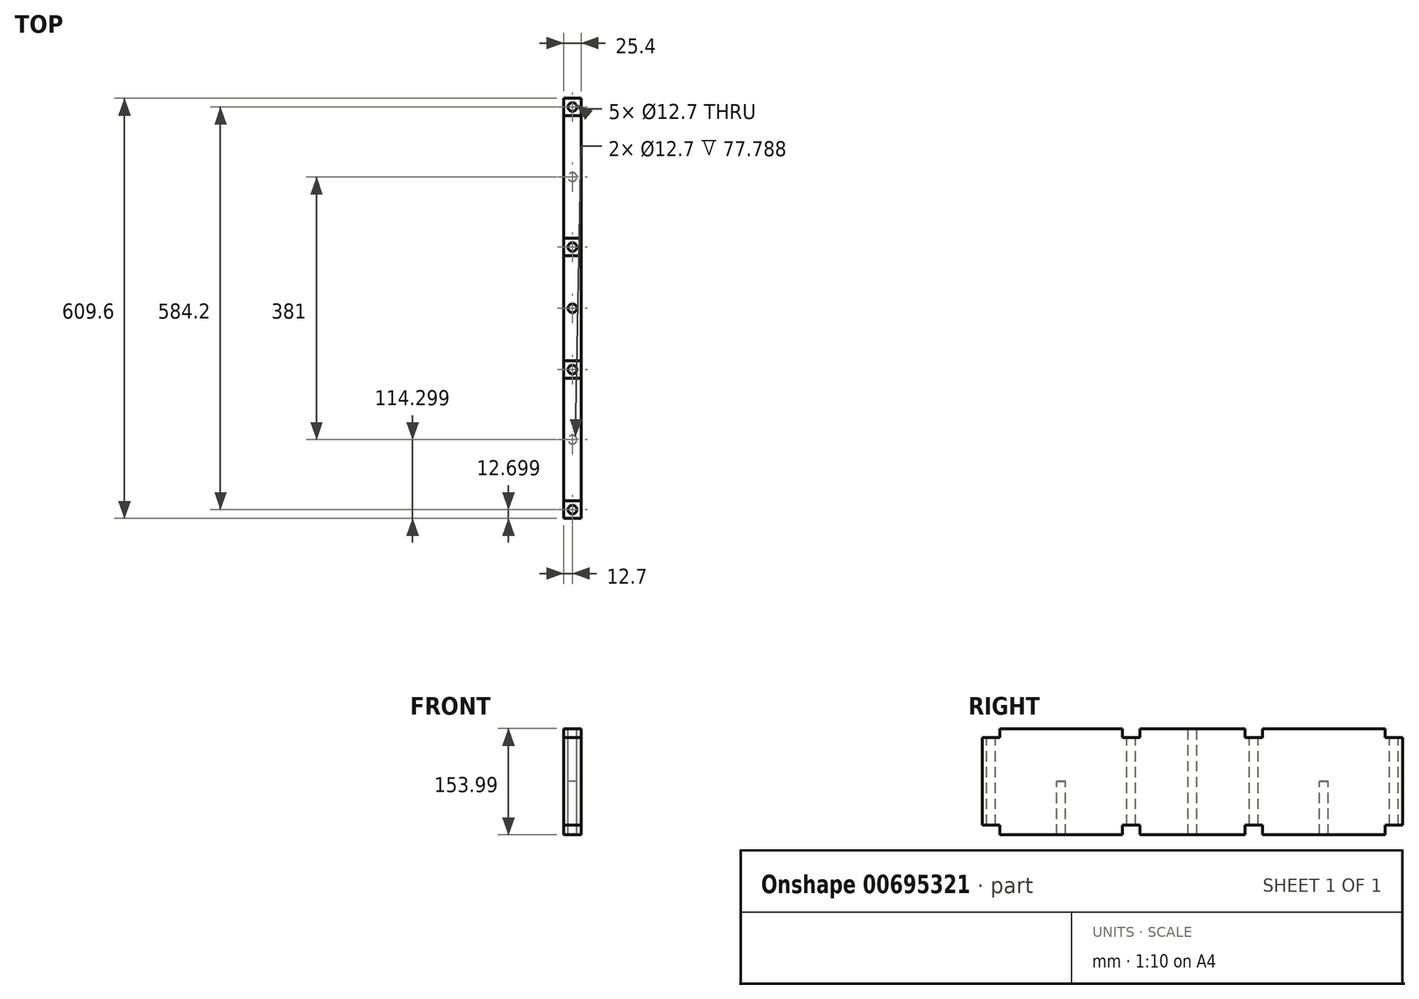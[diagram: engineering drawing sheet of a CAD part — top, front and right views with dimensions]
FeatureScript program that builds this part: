
annotation { "Feature Type Name" : "Feature", "Feature Type Description" : "" }
export const myFeature = defineFeature(function(context is Context, id is Id, definition is map)
    precondition{}
    {
        {
            var Q0;
            Q0=qCreatedBy(makeId("Right.planeOp"),FACE);
            var sketch = newSketch(context, id + "F0", { "sketchPlane" : qUnion([Q0])});
            skLineSegment(sketch, "E0.bottom", {"start": v(-308, -56.05) * mm, "end": v(301.6, -56.05) * mm});
            skLineSegment(sketch, "E0.top", {"start": v(-308, -210.04) * mm, "end": v(301.6, -210.04) * mm});
            skLineSegment(sketch, "E0.left", {"start": v(-308, -56.05) * mm, "end": v(-308, -210.04) * mm});
            skLineSegment(sketch, "E0.right", {"start": v(301.6, -56.05) * mm, "end": v(301.6, -210.04) * mm});
            skSolve(sketch);
        }
        {
            var Q0;
            Q0=makeQuery(id+"F0.imprint","IMPRINT",FACE,{"disambiguationData":[TD([[makeQuery(id+"F0.imprint","IMPRINT",EDGE,{"derivedFrom":sQuery(id+"F0.wireOp",EDGE,"E0.bottom")}),-1.0]])]});
            extrude(context, id + "F1", {"entities" : qUnion([Q0]), "depth" : 25.4 * mm, "offsetDistance" : 25.4 * mm});
        }
        {
            var Q0;
            Q0=makeQuery(id+"F1.opExtrude","CAP_FACE",FACE,{"disambiguationData":[OSD([sQuery(id+"F0.wireOp",EDGE,"E0.bottom"),sQuery(id+"F0.wireOp",EDGE,"E0.top"),sQuery(id+"F0.wireOp",EDGE,"E0.left"),sQuery(id+"F0.wireOp",EDGE,"E0.right")])],"isStart":false});
            var sketch = newSketch(context, id + "F2", { "sketchPlane" : qUnion([Q0])});
            skLineSegment(sketch, "E1.bottom", {"start": v(-308, -210.04) * mm, "end": v(-282.6, -210.04) * mm});
            skLineSegment(sketch, "E1.top", {"start": v(-308, -194.17) * mm, "end": v(-282.6, -194.17) * mm});
            skLineSegment(sketch, "E1.left", {"start": v(-308, -210.04) * mm, "end": v(-308, -194.17) * mm});
            skLineSegment(sketch, "E1.right", {"start": v(-282.6, -210.04) * mm, "end": v(-282.6, -194.17) * mm});
            skLineSegment(sketch, "E2.bottom", {"start": v(-104.8, -210.04) * mm, "end": v(-79.4, -210.04) * mm});
            skLineSegment(sketch, "E2.top", {"start": v(-104.8, -194.17) * mm, "end": v(-79.4, -194.17) * mm});
            skLineSegment(sketch, "E2.left", {"start": v(-104.8, -210.04) * mm, "end": v(-104.8, -194.17) * mm});
            skLineSegment(sketch, "E2.right", {"start": v(-79.4, -210.04) * mm, "end": v(-79.4, -194.17) * mm});
            skLineSegment(sketch, "E3.bottom", {"start": v(73, -210.04) * mm, "end": v(98.4, -210.04) * mm});
            skLineSegment(sketch, "E3.top", {"start": v(73, -194.17) * mm, "end": v(98.4, -194.17) * mm});
            skLineSegment(sketch, "E3.left", {"start": v(73, -210.04) * mm, "end": v(73, -194.17) * mm});
            skLineSegment(sketch, "E3.right", {"start": v(98.4, -210.04) * mm, "end": v(98.4, -194.17) * mm});
            skLineSegment(sketch, "E4.bottom", {"start": v(301.6, -210.04) * mm, "end": v(276.2, -210.04) * mm});
            skLineSegment(sketch, "E4.top", {"start": v(301.6, -194.17) * mm, "end": v(276.2, -194.17) * mm});
            skLineSegment(sketch, "E4.left", {"start": v(301.6, -210.04) * mm, "end": v(301.6, -194.17) * mm});
            skLineSegment(sketch, "E4.right", {"start": v(276.2, -210.04) * mm, "end": v(276.2, -194.17) * mm});
            skLineSegment(sketch, "E5.bottom", {"start": v(-308, -56.05) * mm, "end": v(-282.6, -56.05) * mm});
            skLineSegment(sketch, "E5.top", {"start": v(-308, -68.75) * mm, "end": v(-282.6, -68.75) * mm});
            skLineSegment(sketch, "E5.left", {"start": v(-308, -56.05) * mm, "end": v(-308, -68.75) * mm});
            skLineSegment(sketch, "E5.right", {"start": v(-282.6, -56.05) * mm, "end": v(-282.6, -68.75) * mm});
            skLineSegment(sketch, "E6.bottom", {"start": v(-104.8, -56.05) * mm, "end": v(-79.4, -56.05) * mm});
            skLineSegment(sketch, "E6.top", {"start": v(-104.8, -68.75) * mm, "end": v(-79.4, -68.75) * mm});
            skLineSegment(sketch, "E6.left", {"start": v(-104.8, -56.05) * mm, "end": v(-104.8, -68.75) * mm});
            skLineSegment(sketch, "E6.right", {"start": v(-79.4, -56.05) * mm, "end": v(-79.4, -68.75) * mm});
            skLineSegment(sketch, "E7.bottom", {"start": v(73, -56.05) * mm, "end": v(98.4, -56.05) * mm});
            skLineSegment(sketch, "E7.top", {"start": v(73, -68.75) * mm, "end": v(98.4, -68.75) * mm});
            skLineSegment(sketch, "E7.left", {"start": v(73, -56.05) * mm, "end": v(73, -68.75) * mm});
            skLineSegment(sketch, "E7.right", {"start": v(98.4, -56.05) * mm, "end": v(98.4, -68.75) * mm});
            skLineSegment(sketch, "E8.bottom", {"start": v(301.6, -56.05) * mm, "end": v(276.2, -56.05) * mm});
            skLineSegment(sketch, "E8.top", {"start": v(301.6, -68.75) * mm, "end": v(276.2, -68.75) * mm});
            skLineSegment(sketch, "E8.left", {"start": v(301.6, -56.05) * mm, "end": v(301.6, -68.75) * mm});
            skLineSegment(sketch, "E8.right", {"start": v(276.2, -56.05) * mm, "end": v(276.2, -68.75) * mm});
            skSolve(sketch);
        }
        {
            var Q0;
            Q0=makeQuery(id+"F2.imprint","IMPRINT",FACE,{"disambiguationData":[TD([[makeQuery(id+"F2.imprint","IMPRINT",EDGE,{"derivedFrom":sQuery(id+"F2.wireOp",EDGE,"E5.bottom")}),-1.0]])]});
            var Q1;
            Q1=makeQuery(id+"F2.imprint","IMPRINT",FACE,{"disambiguationData":[TD([[makeQuery(id+"F2.imprint","IMPRINT",EDGE,{"derivedFrom":sQuery(id+"F2.wireOp",EDGE,"E1.bottom")}),1.0]])]});
            var Q2;
            Q2=makeQuery(id+"F2.imprint","IMPRINT",FACE,{"disambiguationData":[TD([[makeQuery(id+"F2.imprint","IMPRINT",EDGE,{"derivedFrom":sQuery(id+"F2.wireOp",EDGE,"E2.bottom")}),1.0]])]});
            var Q3;
            Q3=makeQuery(id+"F2.imprint","IMPRINT",FACE,{"disambiguationData":[TD([[makeQuery(id+"F2.imprint","IMPRINT",EDGE,{"derivedFrom":sQuery(id+"F2.wireOp",EDGE,"E6.bottom")}),-1.0]])]});
            var Q4;
            Q4=makeQuery(id+"F2.imprint","IMPRINT",FACE,{"disambiguationData":[TD([[makeQuery(id+"F2.imprint","IMPRINT",EDGE,{"derivedFrom":sQuery(id+"F2.wireOp",EDGE,"E7.bottom")}),-1.0]])]});
            var Q5;
            Q5=makeQuery(id+"F2.imprint","IMPRINT",FACE,{"disambiguationData":[TD([[makeQuery(id+"F2.imprint","IMPRINT",EDGE,{"derivedFrom":sQuery(id+"F2.wireOp",EDGE,"E3.bottom")}),1.0]])]});
            var Q6;
            Q6=makeQuery(id+"F2.imprint","IMPRINT",FACE,{"disambiguationData":[TD([[makeQuery(id+"F2.imprint","IMPRINT",EDGE,{"derivedFrom":sQuery(id+"F2.wireOp",EDGE,"E8.bottom")}),-1.0]])]});
            var Q7;
            Q7=makeQuery(id+"F2.imprint","IMPRINT",FACE,{"disambiguationData":[TD([[makeQuery(id+"F2.imprint","IMPRINT",EDGE,{"derivedFrom":sQuery(id+"F2.wireOp",EDGE,"E4.bottom")}),1.0]])]});
            extrude(context, id + "F3", {"entities" : qUnion([Q0, Q1, Q2, Q3, Q4, Q5, Q6, Q7]), "operationType" : NewBodyOperationType.REMOVE, "oppositeDirection" : true, "depth" : 25.4 * mm, "offsetDistance" : 25.4 * mm});
        }
        {
            var Q0;
            Q0=makeQuery(id+"F3.boolean.opBoolean","COPY",FACE,{"derivedFrom":makeQuery(id+"F3.opExtrude","SWEPT_FACE",FACE,{"disambiguationData":[OSD([sQuery(id+"F2.wireOp",EDGE,"E5.top")])]})});
            var sketch = newSketch(context, id + "F4", { "sketchPlane" : qUnion([Q0])});
            skCircle(sketch, "E9", {"center": v(12.7, -295.3) * mm, "radius": 6.35 * mm});
            skPoint(sketch, "E9.centerSnap0", {"position": v(25.4, -295.3) * mm});
            skPoint(sketch, "E9.centerSnap1", {"position": v(12.7, -308) * mm});
            skSolve(sketch);
        }
        {
            var Q0;
            Q0=makeQuery(id+"F3.boolean.opBoolean","COPY",FACE,{"derivedFrom":makeQuery(id+"F3.opExtrude","SWEPT_FACE",FACE,{"disambiguationData":[OSD([sQuery(id+"F2.wireOp",EDGE,"E6.top")])]})});
            var sketch = newSketch(context, id + "F5", { "sketchPlane" : qUnion([Q0])});
            skCircle(sketch, "E10", {"center": v(12.7, -92.1) * mm, "radius": 6.35 * mm});
            skPoint(sketch, "E10.centerSnap0", {"position": v(25.4, -92.1) * mm});
            skPoint(sketch, "E10.centerSnap1", {"position": v(12.7, -79.4) * mm});
            skSolve(sketch);
        }
        {
            var Q0;
            Q0=makeQuery(id+"F3.boolean.opBoolean","COPY",FACE,{"derivedFrom":makeQuery(id+"F3.opExtrude","SWEPT_FACE",FACE,{"disambiguationData":[OSD([sQuery(id+"F2.wireOp",EDGE,"E7.top")])]})});
            var sketch = newSketch(context, id + "F6", { "sketchPlane" : qUnion([Q0])});
            skCircle(sketch, "E11", {"center": v(12.7, 85.7) * mm, "radius": 6.35 * mm});
            skPoint(sketch, "E11.centerSnap0", {"position": v(25.4, 85.7) * mm});
            skPoint(sketch, "E11.centerSnap1", {"position": v(12.7, 98.4) * mm});
            skSolve(sketch);
        }
        {
            var Q0;
            Q0=makeQuery(id+"F3.boolean.opBoolean","COPY",FACE,{"derivedFrom":makeQuery(id+"F3.opExtrude","SWEPT_FACE",FACE,{"disambiguationData":[OSD([sQuery(id+"F2.wireOp",EDGE,"E8.top")])]})});
            var sketch = newSketch(context, id + "F7", { "sketchPlane" : qUnion([Q0])});
            skCircle(sketch, "E12", {"center": v(12.7, 288.9) * mm, "radius": 6.35 * mm});
            skPoint(sketch, "E12.centerSnap0", {"position": v(25.4, 288.9) * mm});
            skPoint(sketch, "E12.centerSnap1", {"position": v(12.7, 301.6) * mm});
            skSolve(sketch);
        }
        {
            var Q0;
            Q0=makeQuery(id+"F7.imprint","IMPRINT",FACE,{"disambiguationData":[TD([[makeQuery(id+"F7.imprint","IMPRINT",EDGE,{"derivedFrom":sQuery(id+"F7.wireOp",EDGE,"E12")}),1.0]])]});
            var Q1;
            Q1=makeQuery(id+"F6.imprint","IMPRINT",FACE,{"disambiguationData":[TD([[makeQuery(id+"F6.imprint","IMPRINT",EDGE,{"derivedFrom":sQuery(id+"F6.wireOp",EDGE,"E11")}),1.0]])]});
            var Q2;
            Q2=makeQuery(id+"F5.imprint","IMPRINT",FACE,{"disambiguationData":[TD([[makeQuery(id+"F5.imprint","IMPRINT",EDGE,{"derivedFrom":sQuery(id+"F5.wireOp",EDGE,"E10")}),1.0]])]});
            var Q3;
            Q3=makeQuery(id+"F4.imprint","IMPRINT",FACE,{"disambiguationData":[TD([[makeQuery(id+"F4.imprint","IMPRINT",EDGE,{"derivedFrom":sQuery(id+"F4.wireOp",EDGE,"E9")}),1.0]])]});
            extrude(context, id + "F8", {"entities" : qUnion([Q0, Q1, Q2, Q3]), "operationType" : NewBodyOperationType.REMOVE, "oppositeDirection" : true, "depth" : 177.8 * mm, "offsetDistance" : 25.4 * mm});
        }
        {
            var Q0;
            Q0=makeQuery(id+"F3.boolean.opBoolean","COPY",FACE,{"derivedFrom":makeQuery(id+"F3.opExtrude","SWEPT_FACE",FACE,{"disambiguationData":[OSD([sQuery(id+"F2.wireOp",EDGE,"E1.top")])]})});
            var Q1;
            Q1=makeQuery(id+"F3.boolean.opBoolean","COPY",FACE,{"derivedFrom":makeQuery(id+"F3.opExtrude","SWEPT_FACE",FACE,{"disambiguationData":[OSD([sQuery(id+"F2.wireOp",EDGE,"E2.top")])]})});
            var Q2;
            Q2=makeQuery(id+"F3.boolean.opBoolean","COPY",FACE,{"derivedFrom":makeQuery(id+"F3.opExtrude","SWEPT_FACE",FACE,{"disambiguationData":[OSD([sQuery(id+"F2.wireOp",EDGE,"E3.top")])]})});
            var Q3;
            Q3=makeQuery(id+"F3.boolean.opBoolean","COPY",FACE,{"derivedFrom":makeQuery(id+"F3.opExtrude","SWEPT_FACE",FACE,{"disambiguationData":[OSD([sQuery(id+"F2.wireOp",EDGE,"E4.top")])]})});
            extrude(context, id + "F9", {"entities" : qUnion([Q0, Q1, Q2, Q3]), "operationType" : NewBodyOperationType.ADD, "depth" : 1.59 * mm, "offsetDistance" : 25.4 * mm});
        }
        {
            var Q0;
            {var subQ3=sQuery(id+"F0.wireOp",EDGE,"E0.bottom");Q0=makeQuery(id+"F3.boolean.opBoolean","SPLIT",FACE,{"disambiguationData":[TD([makeQuery(id+"F3.opExtrude","SWEPT_FACE",FACE,{"disambiguationData":[OSD([sQuery(id+"F2.wireOp",EDGE,"E7.right")])]})])],"derivedFrom":makeQuery(id+"F1.opExtrude","SWEPT_FACE",FACE,{"disambiguationData":[OSD([subQ3])]})});}
            var sketch = newSketch(context, id + "F10", { "sketchPlane" : qUnion([Q0])});
            skCircle(sketch, "E13", {"center": v(12.7, 187.3) * mm, "radius": 6.35 * mm});
            skPoint(sketch, "E13.centerSnap0", {"position": v(0, 187.3) * mm});
            skPoint(sketch, "E13.centerSnap1", {"position": v(12.7, 276.2) * mm});
            skSolve(sketch);
        }
        {
            var Q0;
            {var subQ3=sQuery(id+"F0.wireOp",EDGE,"E0.bottom");Q0=makeQuery(id+"F3.boolean.opBoolean","SPLIT",FACE,{"disambiguationData":[TD([makeQuery(id+"F3.opExtrude","SWEPT_FACE",FACE,{"disambiguationData":[OSD([sQuery(id+"F2.wireOp",EDGE,"E6.right")])]})])],"derivedFrom":makeQuery(id+"F1.opExtrude","SWEPT_FACE",FACE,{"disambiguationData":[OSD([subQ3])]})});}
            var sketch = newSketch(context, id + "F11", { "sketchPlane" : qUnion([Q0])});
            skCircle(sketch, "E14", {"center": v(12.7, -3.2) * mm, "radius": 6.35 * mm});
            skPoint(sketch, "E14.centerSnap0", {"position": v(12.7, 73) * mm});
            skPoint(sketch, "E14.centerSnap1", {"position": v(0, -3.2) * mm});
            skSolve(sketch);
        }
        {
            var Q0;
            {var subQ3=sQuery(id+"F0.wireOp",EDGE,"E0.bottom");Q0=makeQuery(id+"F3.boolean.opBoolean","SPLIT",FACE,{"disambiguationData":[TD([makeQuery(id+"F3.opExtrude","SWEPT_FACE",FACE,{"disambiguationData":[OSD([sQuery(id+"F2.wireOp",EDGE,"E5.right")])]})])],"derivedFrom":makeQuery(id+"F1.opExtrude","SWEPT_FACE",FACE,{"disambiguationData":[OSD([subQ3])]})});}
            var sketch = newSketch(context, id + "F12", { "sketchPlane" : qUnion([Q0])});
            skCircle(sketch, "E15", {"center": v(12.7, -193.7) * mm, "radius": 6.35 * mm});
            skPoint(sketch, "E15.centerSnap0", {"position": v(0, -193.7) * mm});
            skPoint(sketch, "E15.centerSnap1", {"position": v(12.7, -104.8) * mm});
            skSolve(sketch);
        }
        {
            var Q0;
            Q0=makeQuery(id+"F12.imprint","IMPRINT",FACE,{"disambiguationData":[TD([[makeQuery(id+"F12.imprint","IMPRINT",EDGE,{"derivedFrom":sQuery(id+"F12.wireOp",EDGE,"E15")}),1.0]])]});
            var Q1;
            Q1=makeQuery(id+"F11.imprint","IMPRINT",FACE,{"disambiguationData":[TD([[makeQuery(id+"F11.imprint","IMPRINT",EDGE,{"derivedFrom":sQuery(id+"F11.wireOp",EDGE,"E14")}),1.0]])]});
            var Q2;
            Q2=makeQuery(id+"F10.imprint","IMPRINT",FACE,{"disambiguationData":[TD([[makeQuery(id+"F10.imprint","IMPRINT",EDGE,{"derivedFrom":sQuery(id+"F10.wireOp",EDGE,"E13")}),1.0]])]});
            extrude(context, id + "F13", {"entities" : qUnion([Q0, Q1, Q2]), "operationType" : NewBodyOperationType.REMOVE, "oppositeDirection" : true, "depth" : 177.8 * mm, "offsetDistance" : 25.4 * mm});
        }
        {
            var Q0;
            {var subQ0=sQuery(id+"F2.wireOp",EDGE,"E4.top");var subQ1=sQuery(id+"F2.wireOp",EDGE,"E3.top");var subQ2=sQuery(id+"F2.wireOp",EDGE,"E2.top");var subQ3=sQuery(id+"F2.wireOp",EDGE,"E1.top");Q0=makeQuery(id+"F9.boolean.opBoolean","MERGE",FACE,{"derivedFrom":[makeQuery(id+"F1.opExtrude","CAP_FACE",FACE,{"disambiguationData":[OSD([sQuery(id+"F0.wireOp",EDGE,"E0.bottom"),sQuery(id+"F0.wireOp",EDGE,"E0.top"),sQuery(id+"F0.wireOp",EDGE,"E0.left"),sQuery(id+"F0.wireOp",EDGE,"E0.right")])],"isStart":false}),makeQuery(id+"F9.opExtrude","SWEPT_FACE",FACE,{"disambiguationData":[OSD([subQ3]),TDD([makeQuery(id+"F3.boolean.opBoolean","COPY",EDGE,{"derivedFrom":makeQuery(id+"F3.opExtrude","CAP_EDGE",EDGE,{"disambiguationData":[OSD([subQ3])],"isStart":true})})])]}),makeQuery(id+"F9.opExtrude","SWEPT_FACE",FACE,{"disambiguationData":[OSD([subQ2]),TDD([makeQuery(id+"F3.boolean.opBoolean","COPY",EDGE,{"derivedFrom":makeQuery(id+"F3.opExtrude","CAP_EDGE",EDGE,{"disambiguationData":[OSD([subQ2])],"isStart":true})})])]}),makeQuery(id+"F9.opExtrude","SWEPT_FACE",FACE,{"disambiguationData":[OSD([subQ1]),TDD([makeQuery(id+"F3.boolean.opBoolean","COPY",EDGE,{"derivedFrom":makeQuery(id+"F3.opExtrude","CAP_EDGE",EDGE,{"disambiguationData":[OSD([subQ1])],"isStart":true})})])]}),makeQuery(id+"F9.opExtrude","SWEPT_FACE",FACE,{"disambiguationData":[OSD([subQ0]),TDD([makeQuery(id+"F3.boolean.opBoolean","COPY",EDGE,{"derivedFrom":makeQuery(id+"F3.opExtrude","CAP_EDGE",EDGE,{"disambiguationData":[OSD([subQ0])],"isStart":true})})])]})]});}
            var sketch = newSketch(context, id + "F14", { "sketchPlane" : qUnion([Q0])});
            skCircle(sketch, "E16", {"center": v(-193.7, -132.25) * mm, "radius": 25.4 * mm});
            skPoint(sketch, "E16.centerSnap0", {"position": v(-308, -132.25) * mm});
            skPoint(sketch, "E16.centerSnap1", {"position": v(-193.7, -56.05) * mm});
            skCircle(sketch, "E17", {"center": v(187.3, -132.25) * mm, "radius": 25.4 * mm});
            skPoint(sketch, "E17.centerSnap0", {"position": v(187.3, -56.05) * mm});
            skPoint(sketch, "E17.centerSnap1", {"position": v(301.6, -132.25) * mm});
            skSolve(sketch);
        }
        {
            var Q0;
            Q0=makeQuery(id+"F14.imprint","IMPRINT",FACE,{"disambiguationData":[TD([[makeQuery(id+"F14.imprint","IMPRINT",EDGE,{"derivedFrom":sQuery(id+"F14.wireOp",EDGE,"E16")}),1.0]])]});
            var Q1;
            Q1=makeQuery(id+"F14.imprint","IMPRINT",FACE,{"disambiguationData":[TD([[makeQuery(id+"F14.imprint","IMPRINT",EDGE,{"derivedFrom":sQuery(id+"F14.wireOp",EDGE,"E17")}),1.0]])]});
            extrude(context, id + "F15", {"entities" : qUnion([Q0, Q1]), "operationType" : NewBodyOperationType.REMOVE, "oppositeDirection" : true, "depth" : 25.4 * mm, "offsetDistance" : 25.4 * mm});
        }
        {
            var Q0;
            Q0=makeQuery(id+"F12.imprint","IMPRINT",FACE,{"disambiguationData":[TD([[makeQuery(id+"F12.imprint","IMPRINT",EDGE,{"derivedFrom":sQuery(id+"F12.wireOp",EDGE,"E15")}),1.0]])]});
            var Q1;
            Q1=makeQuery(id+"F10.imprint","IMPRINT",FACE,{"disambiguationData":[TD([[makeQuery(id+"F10.imprint","IMPRINT",EDGE,{"derivedFrom":sQuery(id+"F10.wireOp",EDGE,"E13")}),1.0]])]});
            extrude(context, id + "F16", {"entities" : qUnion([Q0, Q1]), "operationType" : NewBodyOperationType.ADD, "oppositeDirection" : true, "depth" : 76.2 * mm, "offsetDistance" : 25.4 * mm});
        }
        {
            var Q0;
            Q0=makeQuery(id+"F14.imprint","IMPRINT",FACE,{"disambiguationData":[TD([[makeQuery(id+"F14.imprint","IMPRINT",EDGE,{"derivedFrom":sQuery(id+"F14.wireOp",EDGE,"E16")}),1.0]])]});
            var Q1;
            Q1=makeQuery(id+"F14.imprint","IMPRINT",FACE,{"disambiguationData":[TD([[makeQuery(id+"F14.imprint","IMPRINT",EDGE,{"derivedFrom":sQuery(id+"F14.wireOp",EDGE,"E17")}),1.0]])]});
            extrude(context, id + "F17", {"entities" : qUnion([Q0, Q1]), "operationType" : NewBodyOperationType.REMOVE, "oppositeDirection" : true, "depth" : 25.4 * mm, "offsetDistance" : 25.4 * mm});
        }
    });
